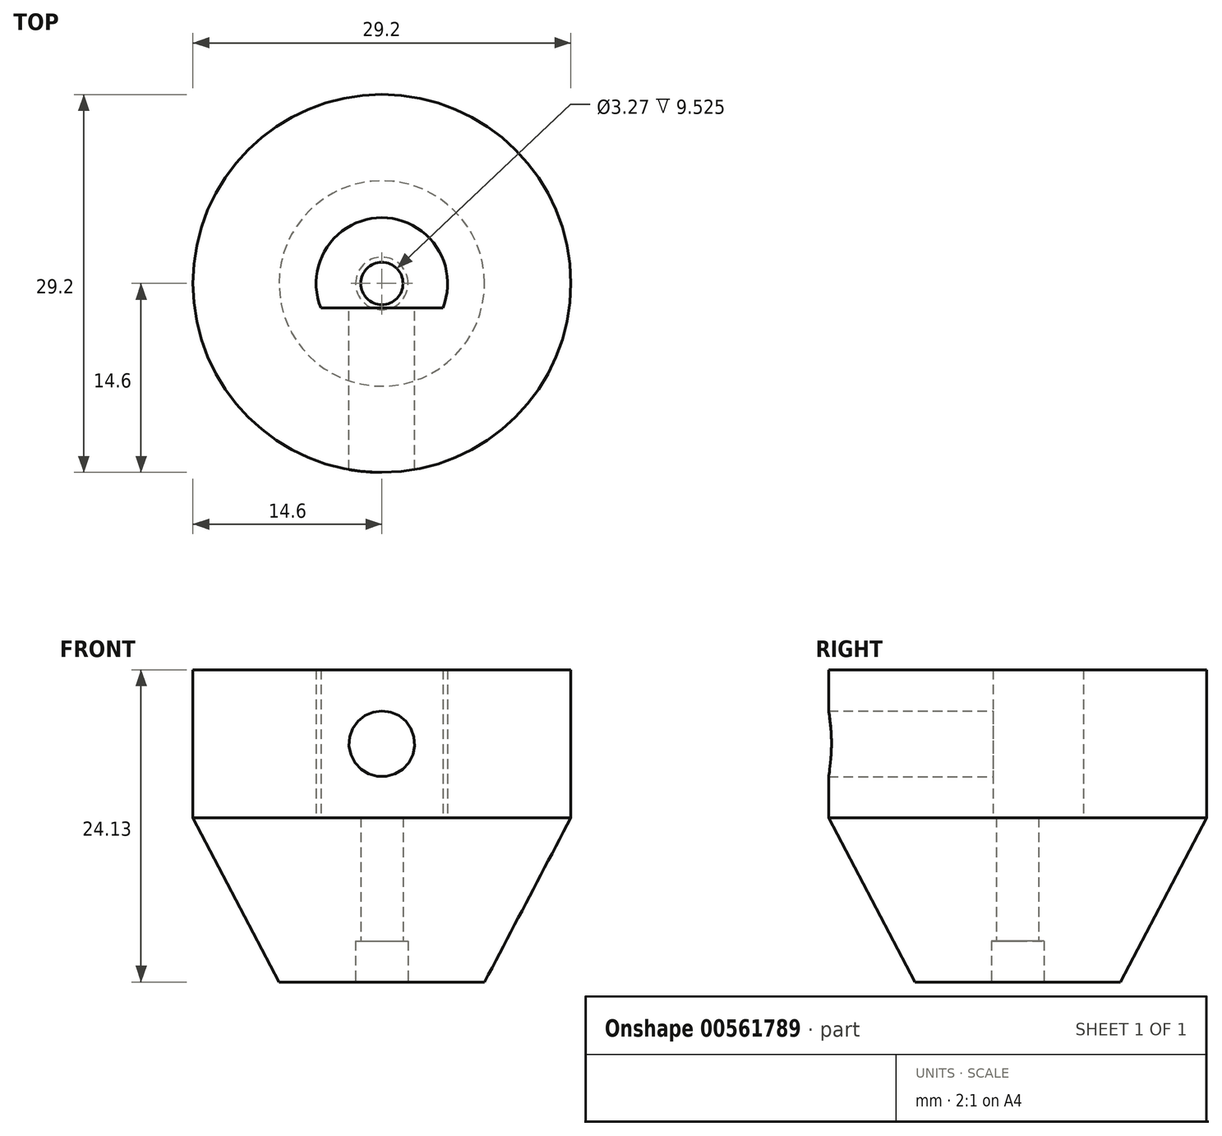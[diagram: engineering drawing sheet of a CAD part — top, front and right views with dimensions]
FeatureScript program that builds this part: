
annotation { "Feature Type Name" : "Feature", "Feature Type Description" : "" }
export const myFeature = defineFeature(function(context is Context, id is Id, definition is map)
    precondition{}
    {
        {
            var Q0;
            Q0=qCreatedBy(makeId("Top.planeOp"),FACE);
            var sketch = newSketch(context, id + "F0", { "sketchPlane" : qUnion([Q0])});
            skArc(sketch, "E0", {"start": v(4.7, -1.9) * mm, "mid": v(0, 5.08) * mm, "end": v(-4.7, -1.9) * mm});
            skLineSegment(sketch, "E1", {"start": v(0, 5.08) * mm, "end": v(17.5, 5.08) * mm, "construction": true});
            skLineSegment(sketch, "E2", {"start": v(17.5, 5.08) * mm, "end": v(17.5, -1.9) * mm, "construction": true});
            skLineSegment(sketch, "E3", {"start": v(4.7, -1.9) * mm, "end": v(-4.7, -1.9) * mm});
            skCircle(sketch, "E4", {"center": v(0, 0) * mm, "radius": 14.6 * mm});
            skSolve(sketch);
        }
        {
            var Q0;
            Q0=makeQuery(id+"F0.imprint","IMPRINT",FACE,{"disambiguationData":[TD([[makeQuery(id+"F0.imprint","IMPRINT",EDGE,{"derivedFrom":sQuery(id+"F0.wireOp",EDGE,"E0")}),-1.0]])]});
            extrude(context, id + "F1", {"entities" : qUnion([Q0]), "depth" : 11.43 * mm, "offsetDistance" : 25.4 * mm});
        }
        {
            var Q0;
            Q0=makeQuery(id+"F1.opExtrude","SWEPT_FACE",FACE,{"disambiguationData":[OSD([sQuery(id+"F0.wireOp",EDGE,"E3")])]});
            var sketch = newSketch(context, id + "F2", { "sketchPlane" : qUnion([Q0])});
            skLineSegment(sketch, "E5", {"start": v(0, 11.43) * mm, "end": v(0, 0) * mm, "construction": true});
            skCircle(sketch, "E6", {"center": v(0, 5.72) * mm, "radius": 2.54 * mm});
            skSolve(sketch);
        }
        {
            var Q0;
            Q0=makeQuery(id+"F2.imprint","IMPRINT",FACE,{"disambiguationData":[TD([[makeQuery(id+"F2.imprint","IMPRINT",EDGE,{"derivedFrom":sQuery(id+"F2.wireOp",EDGE,"E6")}),1.0]])]});
            var Q1;
            Q1=makeQuery(id+"F1.opExtrude","SWEPT_FACE",FACE,{"disambiguationData":[OSD([sQuery(id+"F0.wireOp",EDGE,"E4")])]});
            extrude(context, id + "F3", {"entities" : qUnion([Q0]), "operationType" : NewBodyOperationType.REMOVE, "endBound" : BoundingType.UP_TO_SURFACE, "oppositeDirection" : true, "depth" : 25.4 * mm, "endBoundEntityFace" : qUnion([Q1]), "offsetDistance" : 25.4 * mm});
        }
        {
            var Q0;
            Q0=qCreatedBy(makeId("Top.planeOp"),FACE);
            cPlane(context, id + "F4", {"entities" : qUnion([Q0]), "cplaneType" : CPlaneType.OFFSET, "offset" : 12.7 * mm, "oppositeDirection" : true, "width" : 152.4 * mm, "height" : 152.4 * mm});
        }
        {
            var Q0;
            Q0=qCreatedBy(id+"F4.planeOp",FACE);
            var sketch = newSketch(context, id + "F5", { "sketchPlane" : qUnion([Q0])});
            skCircle(sketch, "E7", {"center": v(0, 0) * mm, "radius": 7.94 * mm});
            skSolve(sketch);
        }
        {
            var Q0;
            Q0=qCreatedBy(makeId("Top.planeOp"),FACE);
            var sketch = newSketch(context, id + "F6", { "sketchPlane" : qUnion([Q0])});
            skLineSegment(sketch, "E8", {"start": v(0, 5.08) * mm, "end": v(30.25, 5.08) * mm, "construction": true});
            skLineSegment(sketch, "E9", {"start": v(30.25, 5.08) * mm, "end": v(30.25, -1.9) * mm, "construction": true});
            skCircle(sketch, "E10", {"center": v(0, 0) * mm, "radius": 14.6 * mm});
            skSolve(sketch);
        }
        {
            var Q1;
            Q1 = qSketchRegion(id + "F5", true);
            var Q2;
            Q2 = qSketchRegion(id + "F6", true);
            loft(context, id + "F7", {"operationType" : NewBodyOperationType.ADD, "sheetProfilesArray" : [{ "sheetProfileEntities" : qUnion([Q1]) }, { "sheetProfileEntities" : qUnion([Q2]) }]});
        }
        {
            var Q0;
            Q0=makeQuery(id+"F7.opLoft","CAP_FACE",FACE,{"disambiguationData":[OSD([makeQuery(id+"F5.imprint","IMPRINT",FACE,{"disambiguationData":[TD([[makeQuery(id+"F5.imprint","IMPRINT",EDGE,{"derivedFrom":sQuery(id+"F5.wireOp",EDGE,"E7")}),1.0]])]})])],"isStart":true});
            var sketch = newSketch(context, id + "F8", { "sketchPlane" : qUnion([Q0])});
            skCircle(sketch, "E11", {"center": v(0, 0) * mm, "radius": 1.64 * mm});
            skCircle(sketch, "E12", {"center": v(0, 0) * mm, "radius": 2.03 * mm});
            skSolve(sketch);
        }
        {
            var Q0;
            Q0=makeQuery(id+"F8.imprint","IMPRINT",FACE,{"disambiguationData":[TD([[makeQuery(id+"F8.imprint","IMPRINT",EDGE,{"derivedFrom":sQuery(id+"F8.wireOp",EDGE,"E11")}),1.0]])]});
            extrude(context, id + "F9", {"entities" : qUnion([Q0]), "operationType" : NewBodyOperationType.REMOVE, "oppositeDirection" : true, "depth" : 25.4 * mm, "offsetDistance" : 25.4 * mm});
        }
        {
            var Q0;
            Q0=makeQuery(id+"F8.imprint","IMPRINT",FACE,{"disambiguationData":[TD([[makeQuery(id+"F8.imprint","IMPRINT",EDGE,{"derivedFrom":sQuery(id+"F8.wireOp",EDGE,"E11")}),-1.0]])]});
            extrude(context, id + "F10", {"entities" : qUnion([Q0]), "operationType" : NewBodyOperationType.REMOVE, "oppositeDirection" : true, "depth" : 3.17 * mm, "offsetDistance" : 25.4 * mm});
        }
    });
